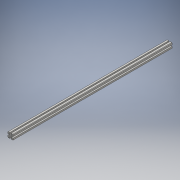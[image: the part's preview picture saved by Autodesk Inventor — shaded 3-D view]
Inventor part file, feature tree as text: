
AUTODESK INVENTOR PART (.ipt)
format: ipt  version: 2016 (Build 200138000, 138)  size: 120,832 bytes
history: native  units: mm
features: extrude x1, sketch x1
ambient origin geometry x8: Origin, YZ Plane, XZ Plane, XY Plane, X Axis, Y Axis, Z Axis, Center Point
bodies: Solid1 (feature_tree)
feature tree (2):
  extrude  "Extrusion1"  [1 undecoded]
  sketch  "Sketch1"  dims[d0=1200.0mm d1=0.0mm]
note: 1 required parameter value undecoded (feature->parameter linkage not recoverable at this tier; creation-order binding heuristic only, values carry confidence <= 0.55)
